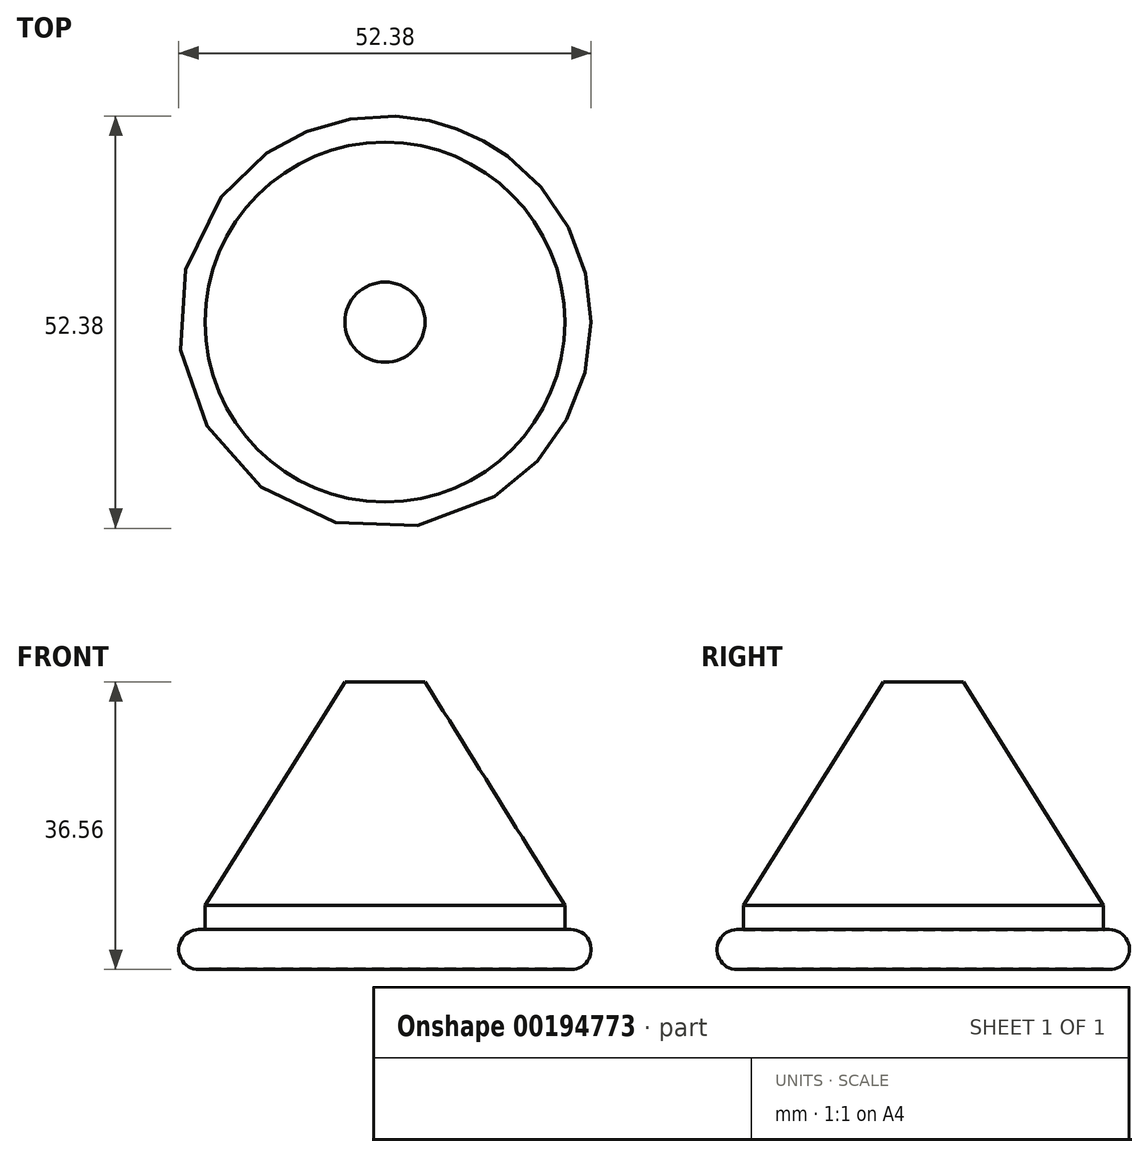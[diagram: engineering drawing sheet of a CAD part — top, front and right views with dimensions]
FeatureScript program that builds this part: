
annotation { "Feature Type Name" : "Feature", "Feature Type Description" : "" }
export const myFeature = defineFeature(function(context is Context, id is Id, definition is map)
    precondition{}
    {
        {
            var Q0;
            Q0=qCreatedBy(makeId("Front.planeOp"),FACE);
            var sketch = newSketch(context, id + "F0", { "sketchPlane" : qUnion([Q0])});
            skLineSegment(sketch, "E0", {"start": v(0, 29.92) * mm, "end": v(0, -20.88) * mm});
            skLineSegment(sketch, "E1", {"start": v(0, -20.88) * mm, "end": v(22.86, -20.88) * mm});
            skLineSegment(sketch, "E2", {"start": v(0, -20.88) * mm, "end": v(0, -16.06) * mm});
            skArc(sketch, "E3", {"start": v(22.86, -20.88) * mm, "mid": v(26.2, -18.47) * mm, "end": v(22.86, -16.06) * mm});
            skLineSegment(sketch, "E4", {"start": v(22.86, -16.06) * mm, "end": v(22.86, -12.88) * mm});
            skLineSegment(sketch, "E5", {"start": v(22.86, -12.88) * mm, "end": v(5.09, 15.55) * mm});
            skArc(sketch, "E6", {"start": v(5.09, 15.55) * mm, "mid": v(9.73, 25.28) * mm, "end": v(0, 29.92) * mm});
            skPoint(sketch, "E7.end.orphan", {"position": v(0, 15.55) * mm});
            skSolve(sketch);
        }
        {
            var Q0;
            Q0=makeQuery(id+"F0.imprint","IMPRINT",FACE,{"disambiguationData":[TD([[makeQuery(id+"F0.imprint","IMPRINT",EDGE,{"derivedFrom":sQuery(id+"F0.wireOp",EDGE,"E0")}),1.0]])]});
            var Q1;
            Q1=sQuery(id+"F0.wireOp",EDGE,"E0");
            revolve(context, id + "F1", {"entities" : qUnion([Q0]), "axis" : qUnion([Q1]), "revolveType" : RevolveType.FULL});
        }
    });
